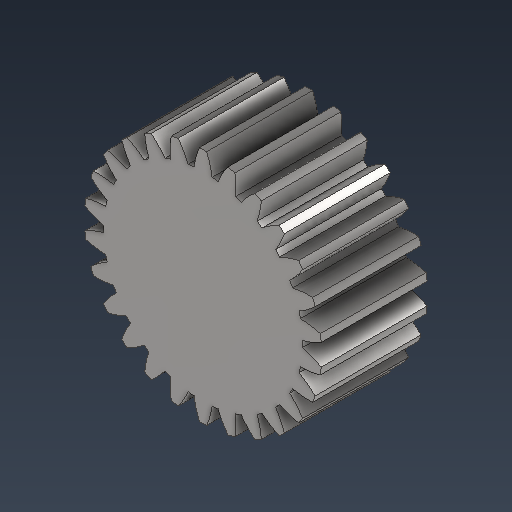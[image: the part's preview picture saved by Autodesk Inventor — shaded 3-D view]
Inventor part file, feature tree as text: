
AUTODESK INVENTOR PART (.ipt)
format: ipt  version: 2021 (Build 250183000, 183)  size: 299,008 bytes
history: native  units: mm (DEFAULTED — no unit token found)
features: plane x3, other x3, sketch x2, extrude x1
ambient origin geometry x8: Origin, YZ Plane, XZ Plane, XY Plane, X Axis, Y Axis, Z Axis, Center Point
bodies: Solid1 (feature_tree)
feature tree (9):
  extrude  "Extrusion1"  Depth=1.25mm TaperAngle=0.0deg
  plane  "Work Plane2"
  plane  "Work Plane8"
  plane  "Work Plane9"
  other  "Engrenagem reta"
  sketch  "Sketch1"  dims[d0=2.8mm d1=1.25mm d2=0.0mm]
  sketch  "Sketch2"  dims[d3=2.6mm d4=10.0mm d5=0.0mm d16=3.0mm d17=0.0mm d34=1.208305mm d39=0.0mm d41=0.0mm d43=3.0mm d46=3.0mm d47=0.0mm d48=0.0mm]
  other  "Srf1"
  other  "Diâmetro do flanco"
